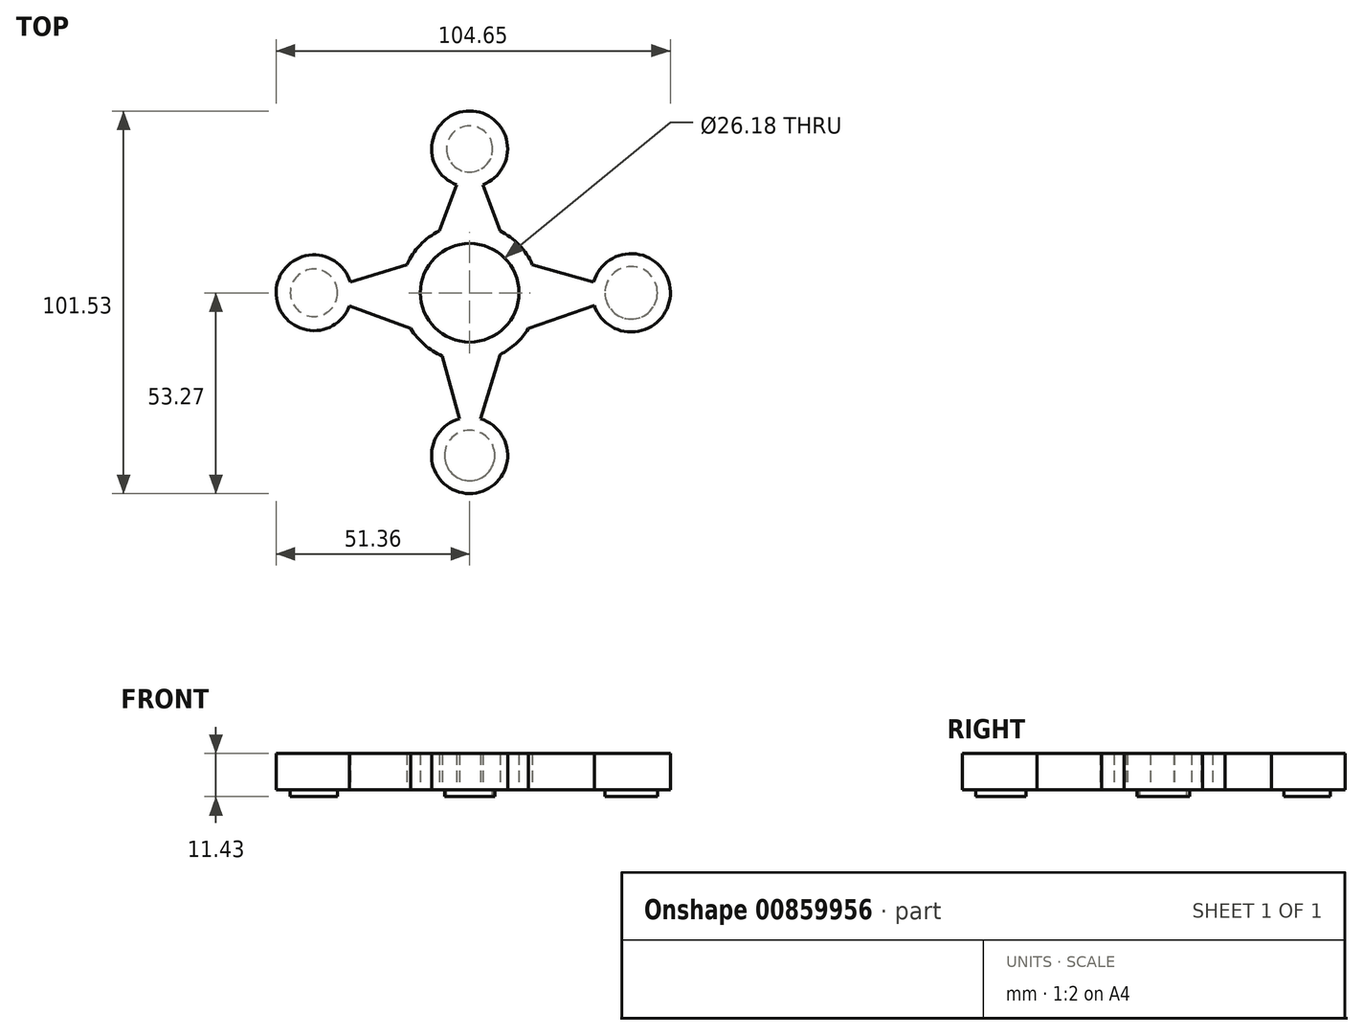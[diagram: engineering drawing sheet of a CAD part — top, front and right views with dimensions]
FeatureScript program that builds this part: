
annotation { "Feature Type Name" : "Feature", "Feature Type Description" : "" }
export const myFeature = defineFeature(function(context is Context, id is Id, definition is map)
    precondition{}
    {
        {
            var Q0;
            Q0=qCreatedBy(makeId("Top.planeOp"),FACE);
            var sketch = newSketch(context, id + "F0", { "sketchPlane" : qUnion([Q0])});
            skCircle(sketch, "E0", {"center": v(0, 0) * mm, "radius": 18.27 * mm});
            skLineSegment(sketch, "E1", {"start": v(0, 38.17) * mm, "end": v(-8.05, 16.4) * mm});
            skLineSegment(sketch, "E2", {"start": v(0, 38.17) * mm, "end": v(8.05, 16.4) * mm});
            skLineSegment(sketch, "E3", {"start": v(-16.66, 7.48) * mm, "end": v(-41.32, 0) * mm});
            skLineSegment(sketch, "E4", {"start": v(-41.32, 0) * mm, "end": v(-15.6, -9.5) * mm});
            skLineSegment(sketch, "E5", {"start": v(-7.26, -16.76) * mm, "end": v(0, -43.15) * mm});
            skLineSegment(sketch, "E6", {"start": v(0, -43.15) * mm, "end": v(8.05, -16.4) * mm});
            skLineSegment(sketch, "E7", {"start": v(16.66, 7.48) * mm, "end": v(42.9, 0) * mm});
            skLineSegment(sketch, "E8", {"start": v(42.9, 0) * mm, "end": v(15.6, -9.5) * mm});
            skSolve(sketch);
        }
        {
            var Q0;
            {var subQ0=sQuery(id+"F0.wireOp",EDGE,"E3");Q0=makeQuery(id+"F0.imprint","IMPRINT",FACE,{"disambiguationData":[TD([[makeQuery(id+"F0.imprint","IMPRINT",EDGE,{"derivedFrom":subQ0}),1.0]])]});}
            var Q1;
            {var subQ0=sQuery(id+"F0.wireOp",EDGE,"E7");Q1=makeQuery(id+"F0.imprint","IMPRINT",FACE,{"disambiguationData":[TD([[makeQuery(id+"F0.imprint","IMPRINT",EDGE,{"derivedFrom":subQ0}),-1.0]])]});}
            var Q2;
            {var subQ0=sQuery(id+"F0.wireOp",EDGE,"E5");Q2=makeQuery(id+"F0.imprint","IMPRINT",FACE,{"disambiguationData":[TD([[makeQuery(id+"F0.imprint","IMPRINT",EDGE,{"derivedFrom":subQ0}),1.0]])]});}
            var Q3;
            {var subQ0=sQuery(id+"F0.wireOp",EDGE,"E0");var subQ4=makeQuery(id+"F0.imprint","INTERSECT",VERTEX,{"derivedFrom":[subQ0,sQuery(id+"F0.wireOp",EDGE,"E2")]});Q3=makeQuery(id+"F0.imprint","IMPRINT",FACE,{"disambiguationData":[TD([[makeQuery(id+"F0.imprint","IMPRINT",EDGE,{"disambiguationData":[TD([[subQ4,1.0]])],"derivedFrom":subQ0}),1.0]])]});}
            var Q4;
            {var subQ0=sQuery(id+"F0.wireOp",EDGE,"E1");Q4=makeQuery(id+"F0.imprint","IMPRINT",FACE,{"disambiguationData":[TD([[makeQuery(id+"F0.imprint","IMPRINT",EDGE,{"derivedFrom":subQ0}),1.0]])]});}
            extrude(context, id + "F1", {"entities" : qUnion([Q0, Q1, Q2, Q3, Q4]), "depth" : 9.65 * mm, "offsetDistance" : 25.4 * mm});
        }
        {
            var Q0;
            Q0=makeQuery(id+"F1.opExtrude","CAP_FACE",FACE,{"disambiguationData":[OSD([sQuery(id+"F0.wireOp",EDGE,"E0"),sQuery(id+"F0.wireOp",EDGE,"E1"),sQuery(id+"F0.wireOp",EDGE,"E2"),sQuery(id+"F0.wireOp",EDGE,"E3"),sQuery(id+"F0.wireOp",EDGE,"E4"),sQuery(id+"F0.wireOp",EDGE,"E5"),sQuery(id+"F0.wireOp",EDGE,"E6"),sQuery(id+"F0.wireOp",EDGE,"E7"),sQuery(id+"F0.wireOp",EDGE,"E8")])],"isStart":true});
            var sketch = newSketch(context, id + "F2", { "sketchPlane" : qUnion([Q0])});
            skCircle(sketch, "E9", {"center": v(0, 0) * mm, "radius": 13.1 * mm});
            skSolve(sketch);
        }
        {
            var Q0;
            Q0 = qSketchRegion(id + "F2", true);
            extrude(context, id + "F3", {"entities" : qUnion([Q0]), "operationType" : NewBodyOperationType.REMOVE, "oppositeDirection" : true, "depth" : 25.4 * mm, "offsetDistance" : 25.4 * mm});
        }
        {
            var Q0;
            Q0=makeQuery(id+"F1.opExtrude","CAP_FACE",FACE,{"disambiguationData":[OSD([sQuery(id+"F0.wireOp",EDGE,"E0"),sQuery(id+"F0.wireOp",EDGE,"E1"),sQuery(id+"F0.wireOp",EDGE,"E2"),sQuery(id+"F0.wireOp",EDGE,"E3"),sQuery(id+"F0.wireOp",EDGE,"E4"),sQuery(id+"F0.wireOp",EDGE,"E5"),sQuery(id+"F0.wireOp",EDGE,"E6"),sQuery(id+"F0.wireOp",EDGE,"E7"),sQuery(id+"F0.wireOp",EDGE,"E8")])],"isStart":true});
            var sketch = newSketch(context, id + "F4", { "sketchPlane" : qUnion([Q0])});
            skCircle(sketch, "E10", {"center": v(0, -38.17) * mm, "radius": 10.1 * mm});
            skCircle(sketch, "E11", {"center": v(-41.32, 0) * mm, "radius": 10.05 * mm});
            skCircle(sketch, "E12", {"center": v(0, 43.15) * mm, "radius": 10.11 * mm});
            skCircle(sketch, "E13", {"center": v(42.9, 0) * mm, "radius": 10.4 * mm});
            skSolve(sketch);
        }
        {
            var Q0;
            {var subQ0=sQuery(id+"F4.wireOp",EDGE,"E10");var subQ1=makeQuery(id+"F1.opExtrude","CAP_EDGE",EDGE,{"disambiguationData":[OSD([sQuery(id+"F0.wireOp",EDGE,"E1")])],"isStart":true});var subQ2=makeQuery(id+"F4.imprint","INTERSECT",VERTEX,{"derivedFrom":[subQ1,subQ0]});Q0=makeQuery(id+"F4.imprint","IMPRINT",FACE,{"disambiguationData":[TD([[makeQuery(id+"F4.imprint","IMPRINT",EDGE,{"disambiguationData":[TD([[subQ2,-1.0]])],"derivedFrom":subQ0}),1.0]])]});}
            extrude(context, id + "F5", {"entities" : qUnion([Q0]), "operationType" : NewBodyOperationType.ADD, "oppositeDirection" : true, "depth" : 9.6 * mm, "offsetDistance" : 25.4 * mm});
        }
        {
            var Q0;
            Q0 = qSketchRegion(id + "F4", true);
            extrude(context, id + "F6", {"entities" : qUnion([Q0]), "operationType" : NewBodyOperationType.ADD, "oppositeDirection" : true, "depth" : 9.65 * mm, "offsetDistance" : 25.4 * mm});
        }
        {
            var Q0;
            {var subQ0=sQuery(id+"F0.wireOp",EDGE,"E2");var subQ1=sQuery(id+"F0.wireOp",EDGE,"E1");Q0=makeQuery(id+"F6.boolean.opBoolean","MERGE",FACE,{"derivedFrom":[makeQuery(id+"F5.boolean.opBoolean","MERGE",FACE,{"derivedFrom":[makeQuery(id+"F1.opExtrude","CAP_FACE",FACE,{"disambiguationData":[OSD([sQuery(id+"F0.wireOp",EDGE,"E0"),subQ1,subQ0,sQuery(id+"F0.wireOp",EDGE,"E3"),sQuery(id+"F0.wireOp",EDGE,"E4"),sQuery(id+"F0.wireOp",EDGE,"E5"),sQuery(id+"F0.wireOp",EDGE,"E6"),sQuery(id+"F0.wireOp",EDGE,"E7"),sQuery(id+"F0.wireOp",EDGE,"E8")])],"isStart":true}),makeQuery(id+"F5.opExtrude","CAP_FACE",FACE,{"disambiguationData":[OSD([subQ1,subQ0,sQuery(id+"F4.wireOp",EDGE,"E10")])],"isStart":true})]}),makeQuery(id+"F6.opExtrude","CAP_FACE",FACE,{"disambiguationData":[OSD([sQuery(id+"F4.wireOp",EDGE,"E11")])],"isStart":true}),makeQuery(id+"F6.opExtrude","CAP_FACE",FACE,{"disambiguationData":[OSD([sQuery(id+"F4.wireOp",EDGE,"E12")])],"isStart":true}),makeQuery(id+"F6.opExtrude","CAP_FACE",FACE,{"disambiguationData":[OSD([sQuery(id+"F4.wireOp",EDGE,"E13")])],"isStart":true})]});}
            var sketch = newSketch(context, id + "F7", { "sketchPlane" : qUnion([Q0])});
            skCircle(sketch, "E14", {"center": v(-41.32, 0) * mm, "radius": 6.27 * mm});
            skCircle(sketch, "E15", {"center": v(0, -38.17) * mm, "radius": 6.13 * mm});
            skCircle(sketch, "E16", {"center": v(0, 43.15) * mm, "radius": 6.69 * mm});
            skCircle(sketch, "E17", {"center": v(42.9, 0) * mm, "radius": 6.96 * mm});
            skSolve(sketch);
        }
        {
            var Q0;
            Q0 = qSketchRegion(id + "F7", true);
            extrude(context, id + "F8", {"entities" : qUnion([Q0]), "operationType" : NewBodyOperationType.ADD, "depth" : 1.78 * mm, "offsetDistance" : 25.4 * mm});
        }
    });
